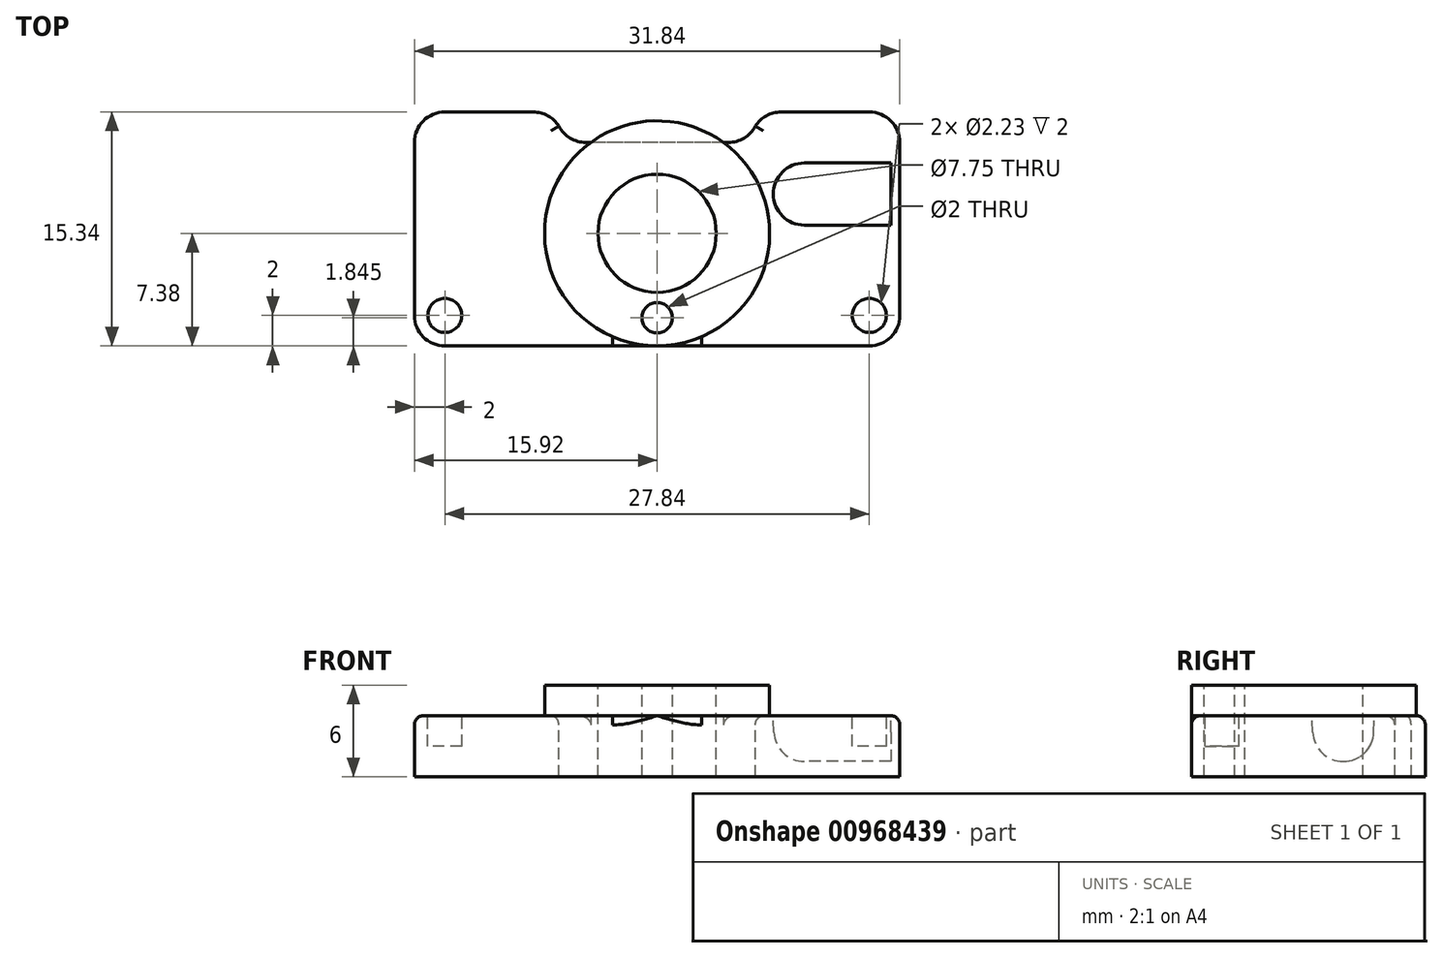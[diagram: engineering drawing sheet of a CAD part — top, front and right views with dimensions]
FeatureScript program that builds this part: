
annotation { "Feature Type Name" : "Feature", "Feature Type Description" : "" }
export const myFeature = defineFeature(function(context is Context, id is Id, definition is map)
    precondition{}
    {
        {
            var Q0;
            Q0=qCreatedBy(makeId("Right.planeOp"),FACE);
            cPlane(context, id + "F0", {"entities" : qUnion([Q0]), "cplaneType" : CPlaneType.OFFSET, "offset" : 9.66 * mm, "width" : 150 * mm, "height" : 150 * mm});
        }
        {
            var Q0;
            Q0=qCreatedBy(makeId("Top.planeOp"),FACE);
            var sketch = newSketch(context, id + "F1", { "sketchPlane" : qUnion([Q0])});
            skCircle(sketch, "E0", {"center": v(0, 0) * mm, "radius": 7.38 * mm});
            skCircle(sketch, "E1", {"center": v(0, 0) * mm, "radius": 3.88 * mm});
            skCircle(sketch, "E2", {"center": v(0, 0) * mm, "radius": 5.54 * mm, "construction": true});
            skLineSegment(sketch, "E3.bottom", {"start": v(13.92, -7.38) * mm, "end": v(-13.92, -7.38) * mm});
            skLineSegment(sketch, "E3.top", {"start": v(13.92, 7.96) * mm, "end": v(8.13, 7.96) * mm});
            skLineSegment(sketch, "E3.left", {"start": v(15.92, -5.38) * mm, "end": v(15.92, 5.96) * mm});
            skLineSegment(sketch, "E3.right", {"start": v(-15.92, -5.38) * mm, "end": v(-15.92, 5.96) * mm});
            skPoint(sketch, "E3.middle", {"position": v(0, 0.29) * mm});
            skPoint(sketch, "E4.visualSharp", {"position": v(-15.92, 7.96) * mm});
            skArc(sketch, "E4.filletArc", {"start": v(-13.92, 7.96) * mm, "mid": v(-15.33, 7.37) * mm, "end": v(-15.92, 5.96) * mm});
            skPoint(sketch, "E5.visualSharp", {"position": v(-15.92, -7.38) * mm});
            skArc(sketch, "E5.filletArc", {"start": v(-15.92, -5.38) * mm, "mid": v(-15.33, -6.8) * mm, "end": v(-13.92, -7.38) * mm});
            skPoint(sketch, "E6.visualSharp", {"position": v(15.92, -7.38) * mm});
            skArc(sketch, "E6.filletArc", {"start": v(13.92, -7.38) * mm, "mid": v(15.33, -6.8) * mm, "end": v(15.92, -5.38) * mm});
            skPoint(sketch, "E7.visualSharp", {"position": v(15.92, 7.96) * mm});
            skArc(sketch, "E7.filletArc", {"start": v(15.92, 5.96) * mm, "mid": v(15.33, 7.37) * mm, "end": v(13.92, 7.96) * mm});
            skArc(sketch, "E8", {"start": v(-6.44, 7.03) * mm, "mid": v(-7.17, 7.71) * mm, "end": v(-8.13, 7.96) * mm});
            skArc(sketch, "E9", {"start": v(-6.44, 7.03) * mm, "mid": v(-5.7, 6.25) * mm, "end": v(-4.67, 5.96) * mm});
            skLineSegment(sketch, "E10", {"start": v(-4.67, 5.96) * mm, "end": v(0, 5.96) * mm});
            skLineSegment(sketch, "E11.MirrorCS", {"start": v(4.67, 5.96) * mm, "end": v(0, 5.96) * mm});
            skArc(sketch, "E12.MirrorCS", {"start": v(6.44, 7.03) * mm, "mid": v(5.7, 6.25) * mm, "end": v(4.67, 5.96) * mm});
            skArc(sketch, "E13.MirrorCS", {"start": v(6.44, 7.03) * mm, "mid": v(7.17, 7.71) * mm, "end": v(8.13, 7.96) * mm});
            skLineSegment(sketch, "E14.trimOffspring", {"start": v(-8.13, 7.96) * mm, "end": v(-13.92, 7.96) * mm});
            skCircle(sketch, "E15", {"center": v(-13.92, -5.38) * mm, "radius": 1.12 * mm});
            skCircle(sketch, "E16", {"center": v(13.92, -5.38) * mm, "radius": 1.12 * mm});
            skCircle(sketch, "E17", {"center": v(0, -5.54) * mm, "radius": 1 * mm});
            skSolve(sketch);
        }
        {
            var Q0;
            Q0=qCreatedBy(id+"F0.planeOp",FACE);
            var sketch = newSketch(context, id + "F2", { "sketchPlane" : qUnion([Q0])});
            skPoint(sketch, "E18.0", {"position": v(-5.38, 0) * mm});
            skArc(sketch, "E19", {"start": v(0.58, -1.08) * mm, "mid": v(2.58, -3) * mm, "end": v(4.58, -1.08) * mm});
            skLineSegment(sketch, "E20", {"start": v(2.58, -3) * mm, "end": v(2.58, 0) * mm});
            skLineSegment(sketch, "E21", {"start": v(0.58, -1.08) * mm, "end": v(0.54, 0) * mm});
            skLineSegment(sketch, "E22", {"start": v(4.58, -1.08) * mm, "end": v(4.62, 0) * mm});
            skLineSegment(sketch, "E23", {"start": v(0.54, 0) * mm, "end": v(4.62, 0) * mm});
            skSolve(sketch);
        }
        {
            var Q0;
            Q0=makeQuery(id+"F1.imprint","IMPRINT",FACE,{"disambiguationData":[TD([[makeQuery(id+"F1.imprint","IMPRINT",EDGE,{"derivedFrom":sQuery(id+"F1.wireOp",EDGE,"E3.top")}),1.0]])]});
            var Q1;
            Q1=makeQuery(id+"F1.imprint","IMPRINT",FACE,{"disambiguationData":[TD([[makeQuery(id+"F1.imprint","IMPRINT",EDGE,{"derivedFrom":sQuery(id+"F1.wireOp",EDGE,"E1")}),-1.0]])]});
            var Q2;
            Q2=makeQuery(id+"F1.imprint","IMPRINT",FACE,{"disambiguationData":[TD([[makeQuery(id+"F1.imprint","IMPRINT",EDGE,{"derivedFrom":sQuery(id+"F1.wireOp",EDGE,"E17")}),1.0]])]});
            var Q3;
            Q3=makeQuery(id+"F1.imprint","IMPRINT",FACE,{"disambiguationData":[TD([[makeQuery(id+"F1.imprint","IMPRINT",EDGE,{"derivedFrom":sQuery(id+"F1.wireOp",EDGE,"E16")}),1.0]])]});
            var Q4;
            Q4=makeQuery(id+"F1.imprint","IMPRINT",FACE,{"disambiguationData":[TD([[makeQuery(id+"F1.imprint","IMPRINT",EDGE,{"derivedFrom":sQuery(id+"F1.wireOp",EDGE,"E3.right")}),-1.0]])]});
            var Q5;
            Q5=makeQuery(id+"F1.imprint","IMPRINT",FACE,{"disambiguationData":[TD([[makeQuery(id+"F1.imprint","IMPRINT",EDGE,{"derivedFrom":sQuery(id+"F1.wireOp",EDGE,"E15")}),1.0]])]});
            extrude(context, id + "F3", {"entities" : qUnion([Q0, Q1, Q2, Q3, Q4, Q5]), "oppositeDirection" : true, "depth" : 4 * mm, "offsetDistance" : 25 * mm});
        }
        {
            var Q0;
            Q0=makeQuery(id+"F1.imprint","IMPRINT",FACE,{"disambiguationData":[TD([[makeQuery(id+"F1.imprint","IMPRINT",EDGE,{"derivedFrom":sQuery(id+"F1.wireOp",EDGE,"E15")}),1.0]])]});
            var Q1;
            Q1=makeQuery(id+"F1.imprint","IMPRINT",FACE,{"disambiguationData":[TD([[makeQuery(id+"F1.imprint","IMPRINT",EDGE,{"derivedFrom":sQuery(id+"F1.wireOp",EDGE,"E16")}),1.0]])]});
            extrude(context, id + "F4", {"entities" : qUnion([Q0, Q1]), "operationType" : NewBodyOperationType.REMOVE, "oppositeDirection" : true, "depth" : 2 * mm, "offsetDistance" : 25 * mm});
        }
        {
            var Q0;
            Q0=makeQuery(id+"F1.imprint","IMPRINT",FACE,{"disambiguationData":[TD([[makeQuery(id+"F1.imprint","IMPRINT",EDGE,{"derivedFrom":sQuery(id+"F1.wireOp",EDGE,"E1")}),-1.0]])]});
            var Q1;
            Q1=makeQuery(id+"F1.imprint","IMPRINT",FACE,{"disambiguationData":[TD([[makeQuery(id+"F1.imprint","IMPRINT",EDGE,{"derivedFrom":sQuery(id+"F1.wireOp",EDGE,"E17")}),1.0]])]});
            var Q2;
            {var subQ0=sQuery(id+"F1.wireOp",EDGE,"E10");var subQ1=sQuery(id+"F1.wireOp",EDGE,"E0");var subQ2=makeQuery(id+"F1.imprint","INTERSECT",VERTEX,{"derivedFrom":[subQ1,subQ0]});Q2=makeQuery(id+"F1.imprint","IMPRINT",FACE,{"disambiguationData":[TD([[makeQuery(id+"F1.imprint","IMPRINT",EDGE,{"disambiguationData":[TD([[subQ2,1.0]])],"derivedFrom":subQ1}),1.0]])]});}
            extrude(context, id + "F5", {"entities" : qUnion([Q0, Q1, Q2]), "operationType" : NewBodyOperationType.ADD, "depth" : 2 * mm, "offsetDistance" : 25 * mm});
        }
        {
            var Q0;
            Q0=makeQuery(id+"F1.imprint","IMPRINT",FACE,{"disambiguationData":[TD([[makeQuery(id+"F1.imprint","IMPRINT",EDGE,{"derivedFrom":sQuery(id+"F1.wireOp",EDGE,"E17")}),1.0]])]});
            extrude(context, id + "F6", {"entities" : qUnion([Q0]), "operationType" : NewBodyOperationType.REMOVE, "endBound" : BoundingType.THROUGH_ALL, "oppositeDirection" : true, "depth" : 25 * mm, "offsetDistance" : 25 * mm, "hasSecondDirection" : true, "secondDirectionBound" : BoundingType.THROUGH_ALL, "secondDirectionOppositeDirection" : false, "secondDirectionDepth" : 25 * mm});
        }
        {
            var Q0;
            {var subQ2=sQuery(id+"F2.wireOp",EDGE,"E20");Q0=makeQuery(id+"F2.imprint","IMPRINT",FACE,{"disambiguationData":[TD([[makeQuery(id+"F2.imprint","IMPRINT",EDGE,{"derivedFrom":subQ2}),-1.0]])]});}
            var Q1;
            Q1=sQuery(id+"F2.wireOp",EDGE,"E20");
            revolve(context, id + "F7", {"operationType" : NewBodyOperationType.REMOVE, "surfaceOperationType" : NewSurfaceOperationType.NEW, "entities" : qUnion([Q0]), "axis" : qUnion([Q1]), "revolveType" : RevolveType.ONE_DIRECTION, "angle" : 180 * degree});
        }
        {
            var Q0;
            Q0 = qSketchRegion(id + "F2", true);
            extrude(context, id + "F8", {"entities" : qUnion([Q0]), "operationType" : NewBodyOperationType.REMOVE, "depth" : (13.92 - 9.66 + 1.4) * mm, "offsetDistance" : 25 * mm});
        }
        {
            var Q0;
            Q0=makeQuery(id+"F3.opExtrude","CAP_EDGE",EDGE,{"disambiguationData":[OSD([sQuery(id+"F1.wireOp",EDGE,"E3.left")])],"isStart":true});
            var Q1;
            Q1=makeQuery(id+"F3.opExtrude","CAP_EDGE",EDGE,{"disambiguationData":[OSD([sQuery(id+"F1.wireOp",EDGE,"E8")])],"isStart":true});
            var Q2;
            Q2=makeQuery(id+"F3.opExtrude","CAP_EDGE",EDGE,{"disambiguationData":[OSD([sQuery(id+"F1.wireOp",EDGE,"E14.trimOffspring")])],"isStart":true});
            var Q3;
            Q3=makeQuery(id+"F3.opExtrude","CAP_EDGE",EDGE,{"disambiguationData":[OSD([sQuery(id+"F1.wireOp",EDGE,"E9")])],"isStart":true});
            var Q4;
            Q4=makeQuery(id+"F3.opExtrude","CAP_EDGE",EDGE,{"disambiguationData":[OSD([sQuery(id+"F1.wireOp",EDGE,"E3.top")])],"isStart":true});
            var Q5;
            Q5=makeQuery(id+"F3.opExtrude","CAP_EDGE",EDGE,{"disambiguationData":[OSD([sQuery(id+"F1.wireOp",EDGE,"E13.MirrorCS")])],"isStart":true});
            var Q6;
            Q6=makeQuery(id+"F3.opExtrude","CAP_EDGE",EDGE,{"disambiguationData":[OSD([sQuery(id+"F1.wireOp",EDGE,"E12.MirrorCS")])],"isStart":true});
            fillet(context, id + "F9", {"entities" : qUnion([Q0, Q1, Q2, Q3, Q4, Q5, Q6]), "tangentPropagation" : true, "radius" : 0.6 * mm, "defaultsChanged" : false, "vertexSettings" : [], "allowEdgeOverflow" : false});
        }
    });
